# Revit family: Faucet-Lavatory-STERLING-Medley-27371_1
name_source: partatom
category: Plumbing Fixtures
units: mm (PartAtom-declared; Revit-internal decimal feet)

## family parameters
Cut with Voids When Loaded = No
Host = Face
OmniClass Number = 23.31.11.00
OmniClass Title = Faucets
Part Type = Normal
Room Calculation Point = No
Round Connector Dimension = Use Diameter
Shared = No

## types (6) — shared parameters
ADA Compliant = Yes
Assembly Code = D2010
CW Connection = Yes
Cold Water Inlet = Cold Water Inlet
Date Modified = 10/13/2022
Default Elevation = 36"
Description = Single-handle bathroom sink faucet
Drain Included = Yes
Flow Rate = 1 GPM
HW Connection = Yes
Handle Clearance = 2 15/16"
Hot Water Inlet = Hot Water Inlet
Length = 5 1/8"
Manufacturer = Sterling Co.
Master Format 2014 = 22 41 39
Master Format 2014 Name = Residential Faucets, Supplies, and Trim
Material = Premium Metal Construction
Pressure = 60.00 psi
Product Documentation Link = https://resources.kohler.com
Product Name = Medley
Product Page URL = http://www.sterlingplumbing.com
Spout Reach = 5 1/8"
URL = https://www.sterlingplumbing.com
Vent Connection = No
Waste Connection = No
Waste Water Outlet = Waste Water Outlet

## per-type parameters (varying)
| type | Finish | Model | Type | WaterSense Certified |
| 1.2 GPM, CP-Polished Chrome | Sterling-Metal-CP-Polished_Chrome | 27371-4-CP | 1 | Yes |
| 1.2 GPM, BN-Vibrant Brushed Nickel | Sterling-Metal-BN-Vibrant_Brushed_Nickel | 27371-4-BN | 3 | Yes |
| 1.2 GPM, BL-Matte Black | Sterling-Metal-BL-Matte_Black | 27371-4-BL | 2 | Yes |
| 0.5 GPM, BL-Matte Black | Sterling-Metal-BL-Matte_Black | 27371-4N-BL | 5 | No |
| 0.5 GPM, BN-Vibrant Brushed Nickel | Sterling-Metal-BN-Vibrant_Brushed_Nickel | 27371-4N-BN | 6 | No |
| 0.5 GPM, CP-Polished Chrome | Sterling-Metal-CP-Polished_Chrome | 27371-4N-CP | 4 | No |

## geometry (parser evidence)
native form markers: Sweep x6
no freeform markers — native parametric forms only
